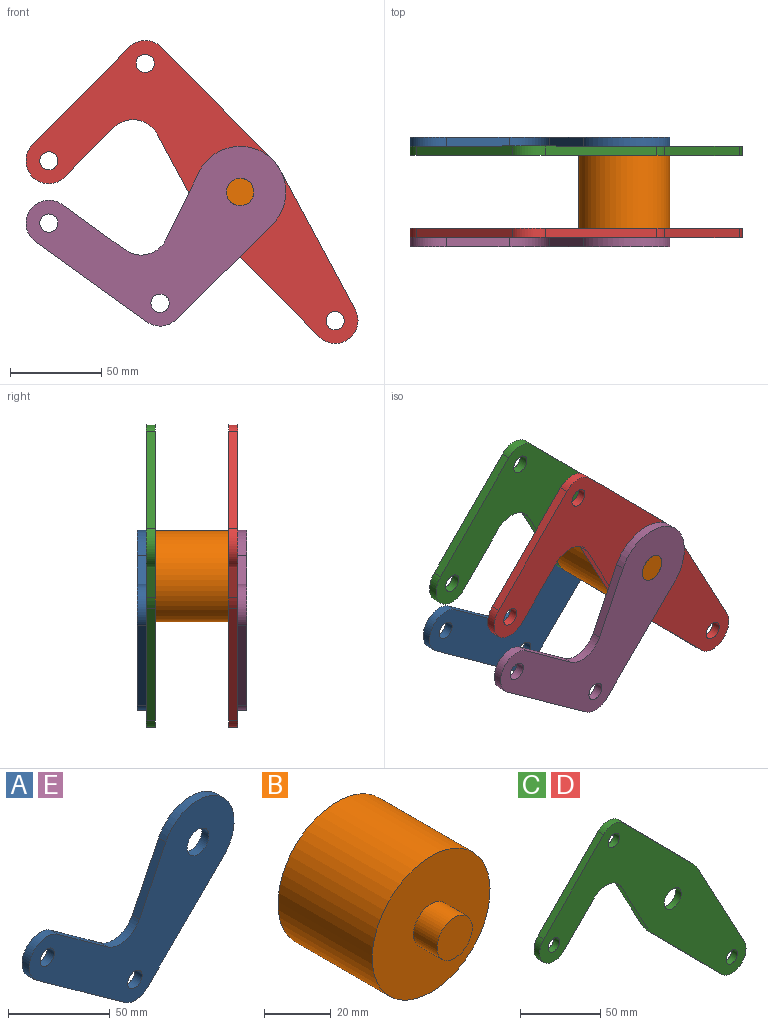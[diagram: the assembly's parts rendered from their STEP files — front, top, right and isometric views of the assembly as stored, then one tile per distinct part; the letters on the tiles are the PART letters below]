
ASSEMBLY  parts=5 mates=2
PART A: 13 faces, bbox 142.2x5x98.4 mm
  f0: cylinder r=25mm len=47.44mm, axis (0,-1,0), area 434.6mm2, adj f1,f8,f11,f12
  f1: plane 37.17x18.26mm, normal (-0.9,0,0.44), area 207.1mm2, adj f0,f2,f11,f12
  f2: cylinder r=15mm len=22.23mm, axis (0,-1,0), area 130.4mm2, adj f1,f3,f11,f12
  f3: plane 34.46x24.81mm, normal (0.58,0,0.81), area 212.3mm2, adj f2,f4,f11,f12
  f4: cylinder r=12.5mm len=22.64mm, axis (0,-1,0), area 196.3mm2, adj f3,f5,f11,f12
  f5: plane 60.86x43.82mm, normal (-0.58,0,-0.81), area 375mm2, adj f4,f6,f11,f12
  f6: cylinder r=12.5mm len=16.09mm, axis (0,-1,0), area 87.7mm2, adj f5,f8,f11,f12
  f7: cylinder r=5mm len=10mm, axis (0,-1,0), area 157.1mm2, adj f11,f12
  f8: plane 52.61x51.97mm, normal (0.7,0,-0.71), area 369.8mm2, adj f0,f6,f11,f12
  f9: cylinder r=7.5mm len=15mm, axis (0,-1,0), area 235.6mm2, adj f11,f12
  f10: cylinder r=5mm len=10mm, axis (0,-1,0), area 157.1mm2, adj f11,f12
  f11: plane 142.19x98.36mm, normal (0,1,0), area 5641.6mm2, adj f0,f1,f2,f3,f4,f5,f6,f7
  f12: plane 142.19x98.36mm, normal (0,-1,0), area 5641.6mm2, adj f0,f1,f2,f3,f4,f5,f6,f7
PART B: 7 faces, bbox 50x60x50 mm
  f0: cylinder r=25mm len=50mm, axis (0,-1,0), area 6283.2mm2, adj f1,f4
  f1: plane 50x50mm, normal (0,-1,0), area 1786.8mm2, adj f0,f3
  f2: plane 15x15mm, normal (0,-1,0), area 176.7mm2, adj f3
  f3: cylinder r=7.5mm len=15mm, axis (0,1,0), area 471.2mm2, adj f1,f2
  f4: plane 50x50mm, normal (0,1,0), area 1786.8mm2, adj f0,f6
  f5: plane 15x15mm, normal (0,1,0), area 176.7mm2, adj f6
  f6: cylinder r=7.5mm len=15mm, axis (0,-1,0), area 471.2mm2, adj f4,f5
PART C: 18 faces, bbox 181.7x5x165.8 mm
  f0: plane 61.6x60.87mm, normal (0.71,0,0.7), area 433mm2, adj f1,f14,f16,f17
  f1: cylinder r=12.5mm len=17.78mm, axis (0,1,0), area 98.9mm2, adj f0,f2,f16,f17
  f2: plane 53.35x52.71mm, normal (-0.71,0,0.7), area 375mm2, adj f1,f3,f16,f17
  f3: cylinder r=12.5mm len=21.39mm, axis (0,1,0), area 196.3mm2, adj f2,f4,f16,f17
  f4: plane 26.86x26.54mm, normal (0.71,0,-0.7), area 188.8mm2, adj f3,f5,f16,f17
  f5: cylinder r=15mm len=23.89mm, axis (0,1,0), area 140.2mm2, adj f4,f6,f16,f17
  f6: plane 43.49x23.35mm, normal (-0.88,0,-0.47), area 246.8mm2, adj f5,f7,f16,f17
  f7: cylinder r=25mm len=5.75mm, axis (0,1,0), area 35.8mm2, adj f6,f8,f16,f17
  f8: plane 61.6x60.87mm, normal (-0.71,0,-0.7), area 433mm2, adj f7,f9,f16,f17
  f9: cylinder r=12.5mm len=21.39mm, axis (0,1,0), area 178.4mm2, adj f8,f10,f16,f17
  f10: plane 76.3x40.96mm, normal (0.88,0,0.47), area 433mm2, adj f9,f14,f16,f17
  f11: cylinder r=5mm len=10mm, axis (0,1,0), area 157.1mm2, adj f16,f17
  f12: cylinder r=5mm len=10mm, axis (0,1,0), area 157.1mm2, adj f16,f17
  f13: cylinder r=7.5mm len=15mm, axis (0,1,0), area 235.6mm2, adj f16,f17
  f14: cylinder r=25mm len=5.75mm, axis (0,1,0), area 35.8mm2, adj f0,f10,f16,f17
  f15: cylinder r=5mm len=10mm, axis (0,1,0), area 157.1mm2, adj f16,f17
  f16: plane 181.66x165.78mm, normal (0,-1,0), area 8612mm2, adj f0,f1,f2,f3,f4,f5,f6,f7
  f17: plane 181.66x165.78mm, normal (0,1,0), area 8612mm2, adj f0,f1,f2,f3,f4,f5,f6,f7
PART D: same geometry as C
PART E: same geometry as A
PLACE A t=(-1.62,6.86,-2.97)mm
PLACE B t=(-1.62,-43.14,-2.97)mm fixed
PLACE C t=(-1.62,6.86,-2.97)mm
PLACE D t=(-1.62,-38.14,-2.97)mm fixed
PLACE E t=(-1.62,-48.14,-2.97)mm
MATE revolute D.f13 <-> E.f0  axis (0,-1,0) through (-1.62,-43.14,-2.97)mm
MATE revolute B.f3 <-> E.f0  axis (0,-1,0) through (-1.62,-48.14,-2.97)mm
